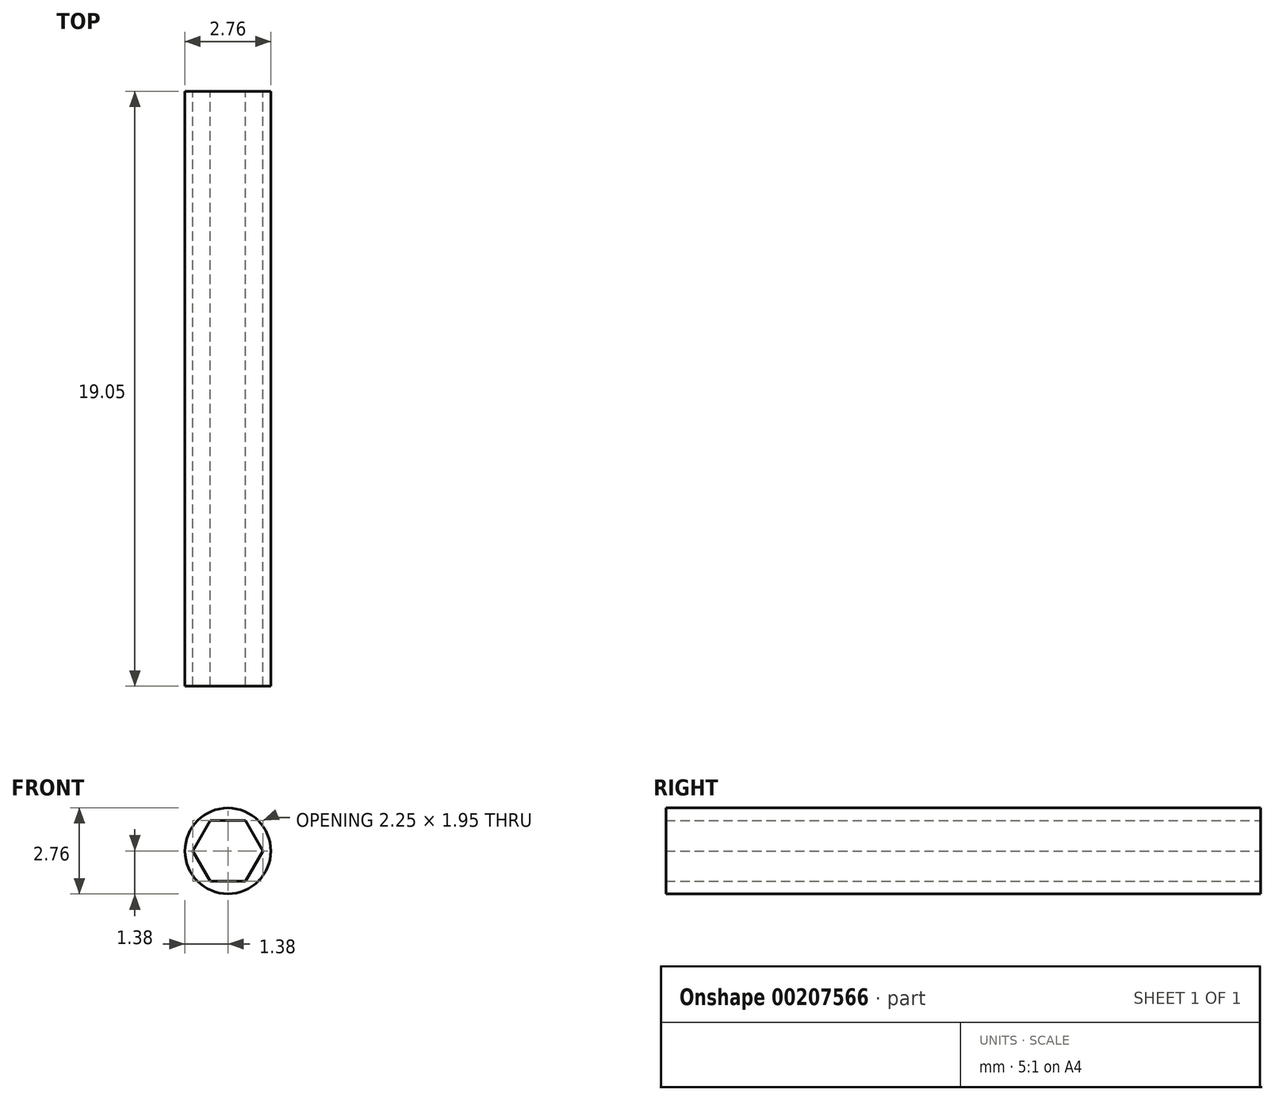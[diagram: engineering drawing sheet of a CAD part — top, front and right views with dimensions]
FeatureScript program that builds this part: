
annotation { "Feature Type Name" : "Feature", "Feature Type Description" : "" }
export const myFeature = defineFeature(function(context is Context, id is Id, definition is map)
    precondition{}
    {
        {
            var Q0;
            Q0=qCreatedBy(makeId("Front.planeOp"),FACE);
            var sketch = newSketch(context, id + "F0", { "sketchPlane" : qUnion([Q0])});
            skCircle(sketch, "E0.cCircle", {"center": v(0, 0) * mm, "radius": 0.97 * mm, "construction": true});
            skLineSegment(sketch, "E0.0", {"start": v(1.13, 0) * mm, "end": v(0.56, -0.98) * mm});
            skLineSegment(sketch, "E0.1", {"start": v(0.56, -0.97) * mm, "end": v(-0.56, -0.97) * mm});
            skLineSegment(sketch, "E0.2", {"start": v(-0.56, -0.98) * mm, "end": v(-1.13, 0) * mm});
            skLineSegment(sketch, "E0.3", {"start": v(-1.13, 0) * mm, "end": v(-0.56, 0.97) * mm});
            skLineSegment(sketch, "E0.4", {"start": v(-0.56, 0.97) * mm, "end": v(0.56, 0.97) * mm});
            skLineSegment(sketch, "E0.5", {"start": v(0.56, 0.97) * mm, "end": v(1.13, 0) * mm});
            skPoint(sketch, "E0.0.midPoint", {"position": v(0.84, -0.49) * mm});
            skLineSegment(sketch, "E1", {"start": v(0, 0.97) * mm, "end": v(0, -0.97) * mm, "construction": true});
            skCircle(sketch, "E2", {"center": v(0, 0) * mm, "radius": 1.38 * mm});
            skLineSegment(sketch, "E3", {"start": v(-1.13, 0) * mm, "end": v(1.13, 0) * mm, "construction": true});
            skSolve(sketch);
        }
        {
            var Q0;
            Q0=makeQuery(id+"F0.imprint","IMPRINT",FACE,{"disambiguationData":[TD([[makeQuery(id+"F0.imprint","IMPRINT",EDGE,{"derivedFrom":sQuery(id+"F0.wireOp",EDGE,"E0.0")}),1.0]])]});
            extrude(context, id + "F1", {"entities" : qUnion([Q0]), "depth" : 19.05 * mm});
        }
    });
